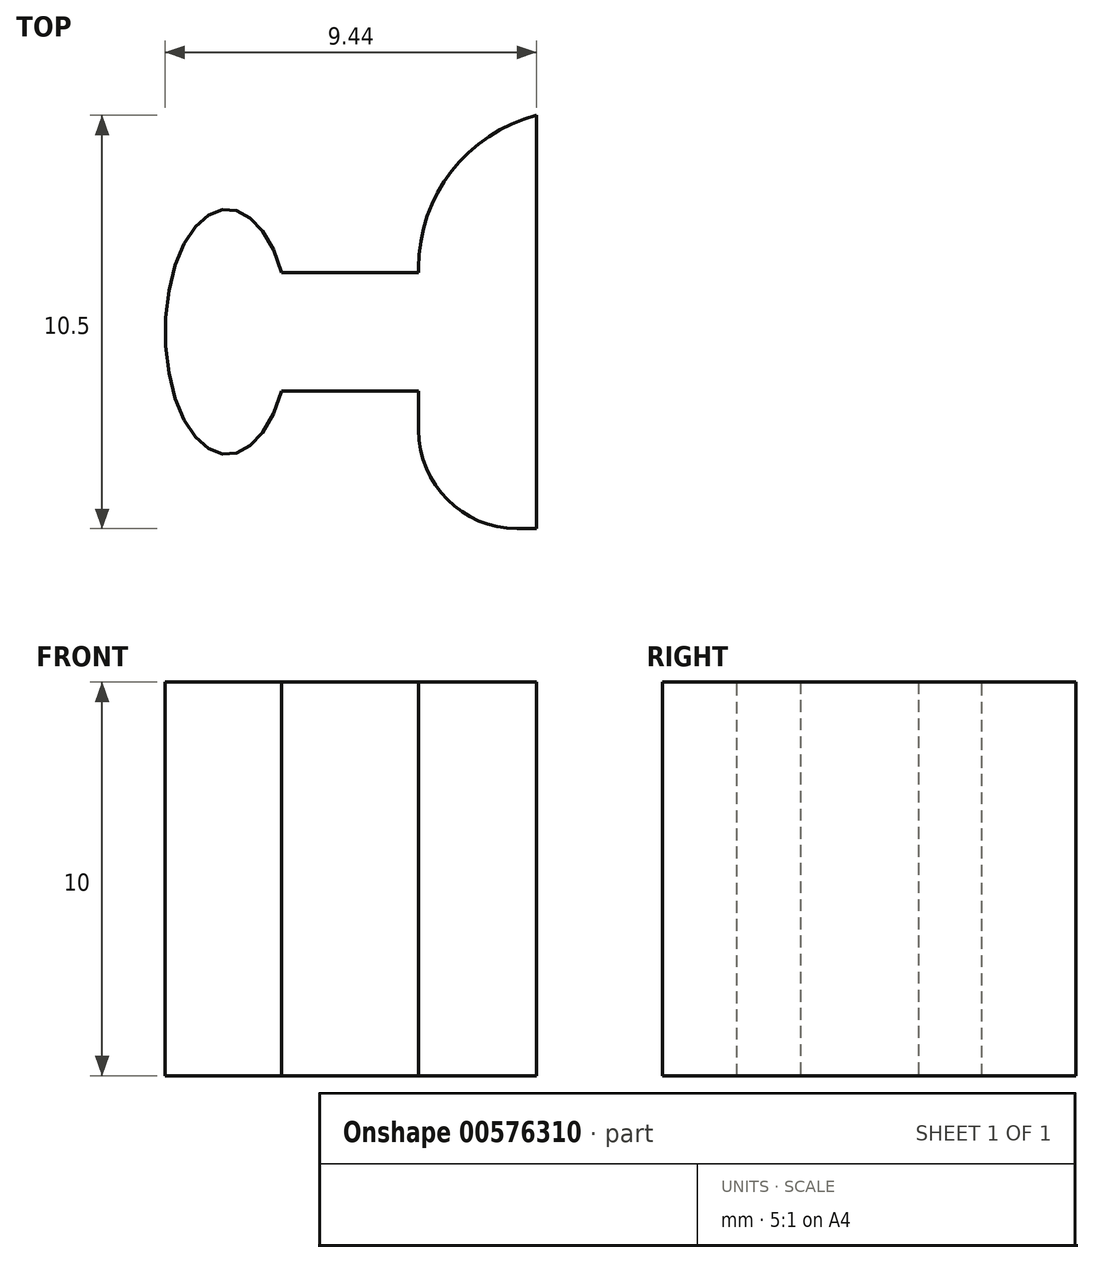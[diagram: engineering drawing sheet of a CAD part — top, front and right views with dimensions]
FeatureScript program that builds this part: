
annotation { "Feature Type Name" : "Feature", "Feature Type Description" : "" }
export const myFeature = defineFeature(function(context is Context, id is Id, definition is map)
    precondition{}
    {
        {
            var Q0;
            Q0=qCreatedBy(makeId("Top.planeOp"),FACE);
            var sketch = newSketch(context, id + "F0", { "sketchPlane" : qUnion([Q0])});
            skLineSegment(sketch, "E0", {"start": v(0, 0) * mm, "end": v(0, 5.25) * mm});
            skLineSegment(sketch, "E1", {"start": v(0, 0) * mm, "end": v(0, -5.25) * mm});
            skLineSegment(sketch, "E2", {"start": v(0, 5.25) * mm, "end": v(-3, 5.25) * mm});
            skLineSegment(sketch, "E3", {"start": v(0, -5.25) * mm, "end": v(-3, -5.25) * mm});
            skLineSegment(sketch, "E4", {"start": v(-3, -5.25) * mm, "end": v(-3, -1.75) * mm});
            skLineSegment(sketch, "E5", {"start": v(-3, 5.25) * mm, "end": v(-3, 1.25) * mm});
            skLineSegment(sketch, "E6", {"start": v(-3, 1.25) * mm, "end": v(-6.5, 1.25) * mm});
            skLineSegment(sketch, "E7", {"start": v(-3, -1.75) * mm, "end": v(-6.5, -1.75) * mm});
            skEllipse(sketch, "E8", {"center": v(-7.86, -0.25) * mm, "majorRadius": 3.12 * mm, "minorRadius": 1.58 * mm, "majorAxis": v(0, -1)});
            skSolve(sketch);
        }
        {
            var Q0;
            Q0=makeQuery(id+"F0.imprint","IMPRINT",FACE,{"disambiguationData":[TD([[makeQuery(id+"F0.imprint","IMPRINT",EDGE,{"derivedFrom":sQuery(id+"F0.wireOp",EDGE,"E0")}),1.0]])]});
            extrude(context, id + "F1", {"entities" : qUnion([Q0]), "depth" : 10 * mm, "offsetDistance" : 25 * mm});
        }
        {
            var Q0;
            {var subQ0=sQuery(id+"F0.wireOp",EDGE,"E8");var subQ1=makeQuery(id+"F0.imprint","INTERSECT",VERTEX,{"derivedFrom":[sQuery(id+"F0.wireOp",EDGE,"E6"),subQ0]});Q0=makeQuery(id+"F0.imprint","IMPRINT",FACE,{"disambiguationData":[TD([[makeQuery(id+"F0.imprint","IMPRINT",EDGE,{"disambiguationData":[TD([[subQ1,1.0]])],"derivedFrom":subQ0}),1.0]])]});}
            extrude(context, id + "F2", {"entities" : qUnion([Q0]), "operationType" : NewBodyOperationType.ADD, "depth" : 10 * mm, "offsetDistance" : 25 * mm});
        }
        {
            var Q0;
            Q0=makeQuery(id+"F1.opExtrude","SWEPT_EDGE",EDGE,{"disambiguationData":[OSD([sQuery(id+"F0.wireOp",EDGE,"E2"),sQuery(id+"F0.wireOp",EDGE,"E5")])]});
            fillet(context, id + "F3", {"entities" : qUnion([Q0]), "radius" : 4 * mm, "tangentPropagation" : true, "allowEdgeOverflow" : false});
        }
        {
            var Q0;
            Q0=makeQuery(id+"F1.opExtrude","SWEPT_EDGE",EDGE,{"disambiguationData":[OSD([sQuery(id+"F0.wireOp",EDGE,"E3"),sQuery(id+"F0.wireOp",EDGE,"E4")])]});
            fillet(context, id + "F4", {"entities" : qUnion([Q0]), "radius" : 2.5 * mm, "tangentPropagation" : true, "allowEdgeOverflow" : false});
        }
    });
